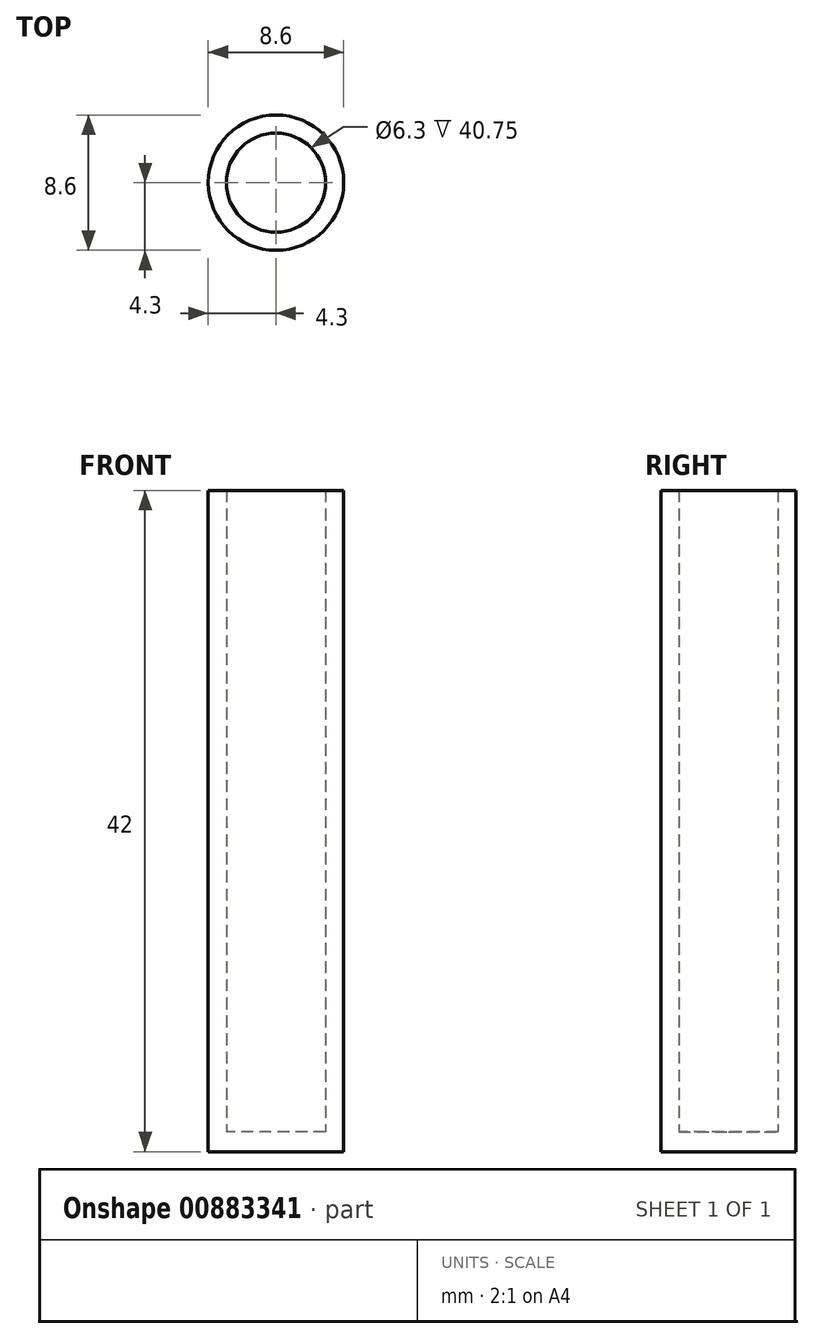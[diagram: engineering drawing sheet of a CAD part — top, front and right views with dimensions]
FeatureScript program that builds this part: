
annotation { "Feature Type Name" : "Feature", "Feature Type Description" : "" }
export const myFeature = defineFeature(function(context is Context, id is Id, definition is map)
    precondition{}
    {
        {
            var Q0;
            Q0=qCreatedBy(makeId("Top.planeOp"),FACE);
            var sketch = newSketch(context, id + "F0", { "sketchPlane" : qUnion([Q0])});
            skCircle(sketch, "E0", {"center": v(0, 0) * mm, "radius": 4.3 * mm});
            skCircle(sketch, "E1", {"center": v(0, 0) * mm, "radius": 3.15 * mm});
            skSolve(sketch);
        }
        {
            var Q0;
            Q0=makeQuery(id+"F0.imprint","IMPRINT",FACE,{"disambiguationData":[TD([[makeQuery(id+"F0.imprint","IMPRINT",EDGE,{"derivedFrom":sQuery(id+"F0.wireOp",EDGE,"E1")}),1.0]])]});
            var Q1;
            Q1=makeQuery(id+"F0.imprint","IMPRINT",FACE,{"disambiguationData":[TD([[makeQuery(id+"F0.imprint","IMPRINT",EDGE,{"derivedFrom":sQuery(id+"F0.wireOp",EDGE,"E0")}),1.0]])]});
            extrude(context, id + "F1", {"entities" : qUnion([Q0, Q1]), "depth" : 1.25 * mm, "offsetDistance" : 25 * mm});
        }
        {
            var Q0;
            Q0 = qSketchRegion(id + "F0", true);
            extrude(context, id + "F2", {"entities" : qUnion([Q0]), "operationType" : NewBodyOperationType.ADD, "depth" : 42 * mm, "offsetDistance" : 25 * mm});
        }
    });
